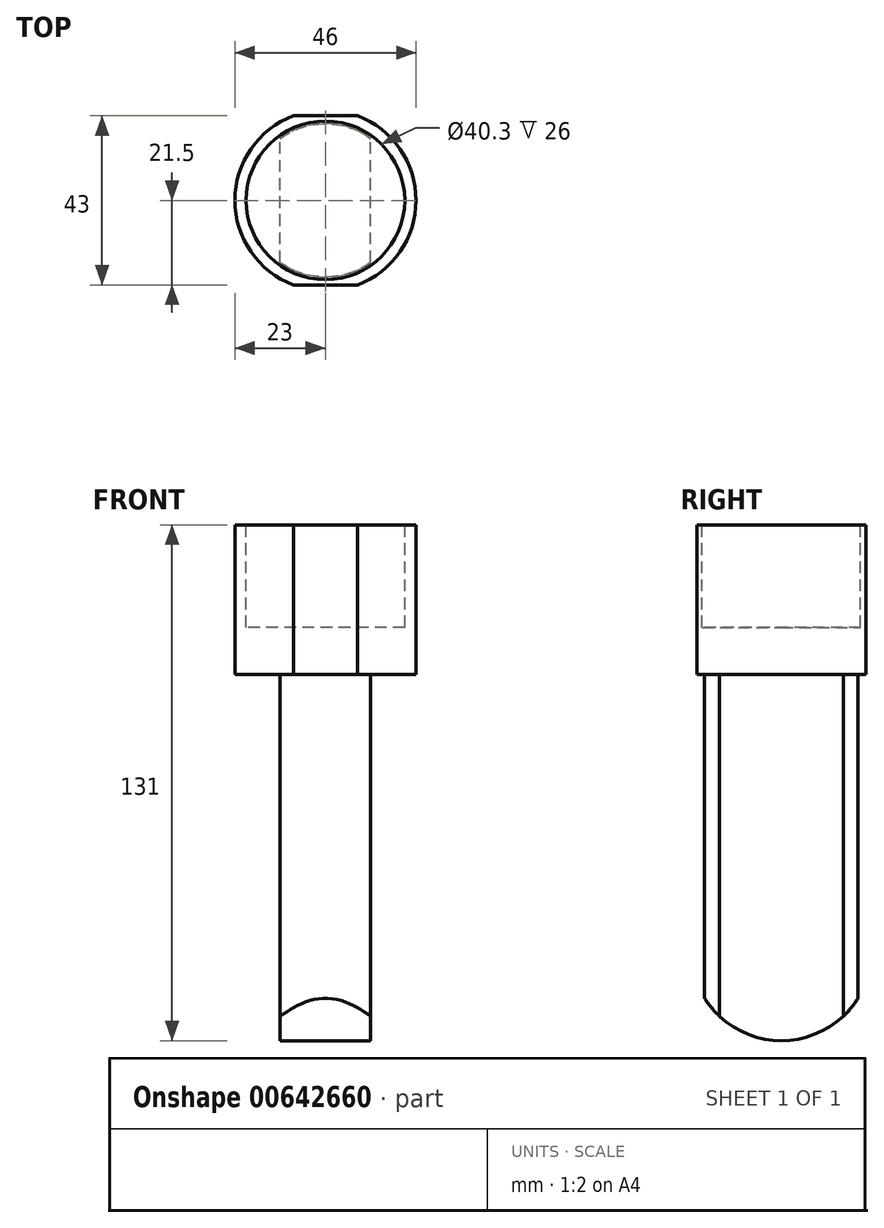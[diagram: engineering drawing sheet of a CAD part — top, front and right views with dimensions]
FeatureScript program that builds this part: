
annotation { "Feature Type Name" : "Feature", "Feature Type Description" : "" }
export const myFeature = defineFeature(function(context is Context, id is Id, definition is map)
    precondition{}
    {
        {
            var Q0;
            Q0=qCreatedBy(makeId("Top.planeOp"),FACE);
            var sketch = newSketch(context, id + "F0", { "sketchPlane" : qUnion([Q0])});
            skArc(sketch, "E0", {"start": v(-8.17, 21.5) * mm, "mid": v(-23, 0) * mm, "end": v(-8.17, -21.5) * mm});
            skLineSegment(sketch, "E1", {"start": v(-8.17, 21.5) * mm, "end": v(8.17, 21.5) * mm});
            skLineSegment(sketch, "E2.MirrorCS", {"start": v(-8.17, -21.5) * mm, "end": v(8.17, -21.5) * mm});
            skArc(sketch, "E3.trimOffspring", {"start": v(8.17, -21.5) * mm, "mid": v(23, 0) * mm, "end": v(8.17, 21.5) * mm});
            skSolve(sketch);
        }
        {
            var Q0;
            Q0=makeQuery(id+"F0.imprint","IMPRINT",FACE,{"disambiguationData":[TD([[makeQuery(id+"F0.imprint","IMPRINT",EDGE,{"derivedFrom":sQuery(id+"F0.wireOp",EDGE,"E0")}),1.0]])]});
            extrude(context, id + "F1", {"entities" : qUnion([Q0]), "depth" : 38 * mm, "offsetDistance" : 25 * mm});
        }
        {
            var Q0;
            Q0=makeQuery(id+"F1.opExtrude","CAP_FACE",FACE,{"disambiguationData":[OSD([sQuery(id+"F0.wireOp",EDGE,"E0"),sQuery(id+"F0.wireOp",EDGE,"E1"),sQuery(id+"F0.wireOp",EDGE,"E2.MirrorCS"),sQuery(id+"F0.wireOp",EDGE,"E3.trimOffspring")])],"isStart":false});
            var sketch = newSketch(context, id + "F2", { "sketchPlane" : qUnion([Q0])});
            skCircle(sketch, "E4", {"center": v(0, 0) * mm, "radius": 20.15 * mm});
            skSolve(sketch);
        }
        {
            var Q0;
            Q0=makeQuery(id+"F2.imprint","IMPRINT",FACE,{"disambiguationData":[TD([[makeQuery(id+"F2.imprint","IMPRINT",EDGE,{"derivedFrom":sQuery(id+"F2.wireOp",EDGE,"E4")}),1.0]])]});
            extrude(context, id + "F3", {"entities" : qUnion([Q0]), "operationType" : NewBodyOperationType.REMOVE, "oppositeDirection" : true, "depth" : 26 * mm, "offsetDistance" : 25 * mm});
        }
        {
            var Q0;
            Q0=makeQuery(id+"F1.opExtrude","CAP_FACE",FACE,{"disambiguationData":[OSD([sQuery(id+"F0.wireOp",EDGE,"E0"),sQuery(id+"F0.wireOp",EDGE,"E1"),sQuery(id+"F0.wireOp",EDGE,"E2.MirrorCS"),sQuery(id+"F0.wireOp",EDGE,"E3.trimOffspring")])],"isStart":true});
            var sketch = newSketch(context, id + "F4", { "sketchPlane" : qUnion([Q0])});
            skArc(sketch, "E5", {"start": v(-11.5, -15.75) * mm, "mid": v(0, -19.5) * mm, "end": v(11.5, -15.75) * mm});
            skLineSegment(sketch, "E6", {"start": v(-11.5, 15.75) * mm, "end": v(-11.5, -15.75) * mm});
            skLineSegment(sketch, "E7.MirrorCS", {"start": v(11.5, 15.75) * mm, "end": v(11.5, -15.75) * mm});
            skArc(sketch, "E8.trimOffspring", {"start": v(11.5, 15.75) * mm, "mid": v(0, 19.5) * mm, "end": v(-11.5, 15.75) * mm});
            skSolve(sketch);
        }
        {
            var Q0;
            Q0=makeQuery(id+"F4.imprint","IMPRINT",FACE,{"disambiguationData":[TD([[makeQuery(id+"F4.imprint","IMPRINT",EDGE,{"derivedFrom":sQuery(id+"F4.wireOp",EDGE,"E5")}),1.0]])]});
            extrude(context, id + "F5", {"entities" : qUnion([Q0]), "operationType" : NewBodyOperationType.ADD, "depth" : 93 * mm, "offsetDistance" : 25 * mm});
        }
        {
            var Q0;
            Q0=makeQuery(id+"F5.opExtrude","SWEPT_FACE",FACE,{"disambiguationData":[OSD([sQuery(id+"F4.wireOp",EDGE,"E7.MirrorCS")])]});
            var sketch = newSketch(context, id + "F6", { "sketchPlane" : qUnion([Q0])});
            skArc(sketch, "E9", {"start": v(-23, -70) * mm, "mid": v(0, -93) * mm, "end": v(23, -70) * mm});
            skLineSegment(sketch, "E10", {"start": v(0, -70) * mm, "end": v(-23, -70) * mm});
            skLineSegment(sketch, "E11", {"start": v(0, -70) * mm, "end": v(23, -70) * mm});
            skLineSegment(sketch, "E12", {"start": v(23, -70) * mm, "end": v(48.18, -96.71) * mm});
            skLineSegment(sketch, "E13", {"start": v(48.18, -96.71) * mm, "end": v(2.27, -108.14) * mm});
            skLineSegment(sketch, "E14", {"start": v(2.27, -108.14) * mm, "end": v(-50.9, -87.27) * mm});
            skLineSegment(sketch, "E15", {"start": v(-50.9, -87.27) * mm, "end": v(-23, -70) * mm});
            skSolve(sketch);
        }
        {
            var Q0;
            {var subQ6=sQuery(id+"F6.wireOp",EDGE,"E12");Q0=makeQuery(id+"F6.imprint","IMPRINT",FACE,{"disambiguationData":[TD([[makeQuery(id+"F6.imprint","IMPRINT",EDGE,{"derivedFrom":subQ6}),-1.0]])]});}
            var Q1;
            {var subQ0=sQuery(id+"F6.wireOp",EDGE,"E9");var subQ1=sQuery(id+"F4.wireOp",EDGE,"E7.MirrorCS");var subQ4=makeQuery(id+"F5.opExtrude","CAP_EDGE",EDGE,{"disambiguationData":[OSD([subQ1])],"isStart":false});var subQ5=makeQuery(id+"F6.imprint","INTERSECT",VERTEX,{"derivedFrom":[subQ4,subQ0]});Q1=makeQuery(id+"F6.imprint","IMPRINT",FACE,{"disambiguationData":[TD([[makeQuery(id+"F6.imprint","IMPRINT",EDGE,{"disambiguationData":[TD([[subQ5,1.0]])],"derivedFrom":subQ0}),-1.0]])]});}
            var Q2;
            {var subQ0=sQuery(id+"F6.wireOp",EDGE,"E9");var subQ1=sQuery(id+"F4.wireOp",EDGE,"E7.MirrorCS");var subQ2=makeQuery(id+"F5.opExtrude","CAP_EDGE",EDGE,{"disambiguationData":[OSD([subQ1])],"isStart":false});var subQ3=makeQuery(id+"F6.imprint","INTERSECT",VERTEX,{"derivedFrom":[subQ2,subQ0]});Q2=makeQuery(id+"F6.imprint","IMPRINT",FACE,{"disambiguationData":[TD([[makeQuery(id+"F6.imprint","IMPRINT",EDGE,{"disambiguationData":[TD([[subQ3,-1.0]])],"derivedFrom":subQ0}),-1.0]])]});}
            extrude(context, id + "F7", {"entities" : qUnion([Q0, Q1, Q2]), "operationType" : NewBodyOperationType.REMOVE, "endBound" : BoundingType.THROUGH_ALL, "oppositeDirection" : true, "depth" : 25 * mm, "offsetDistance" : 25 * mm});
        }
    });
